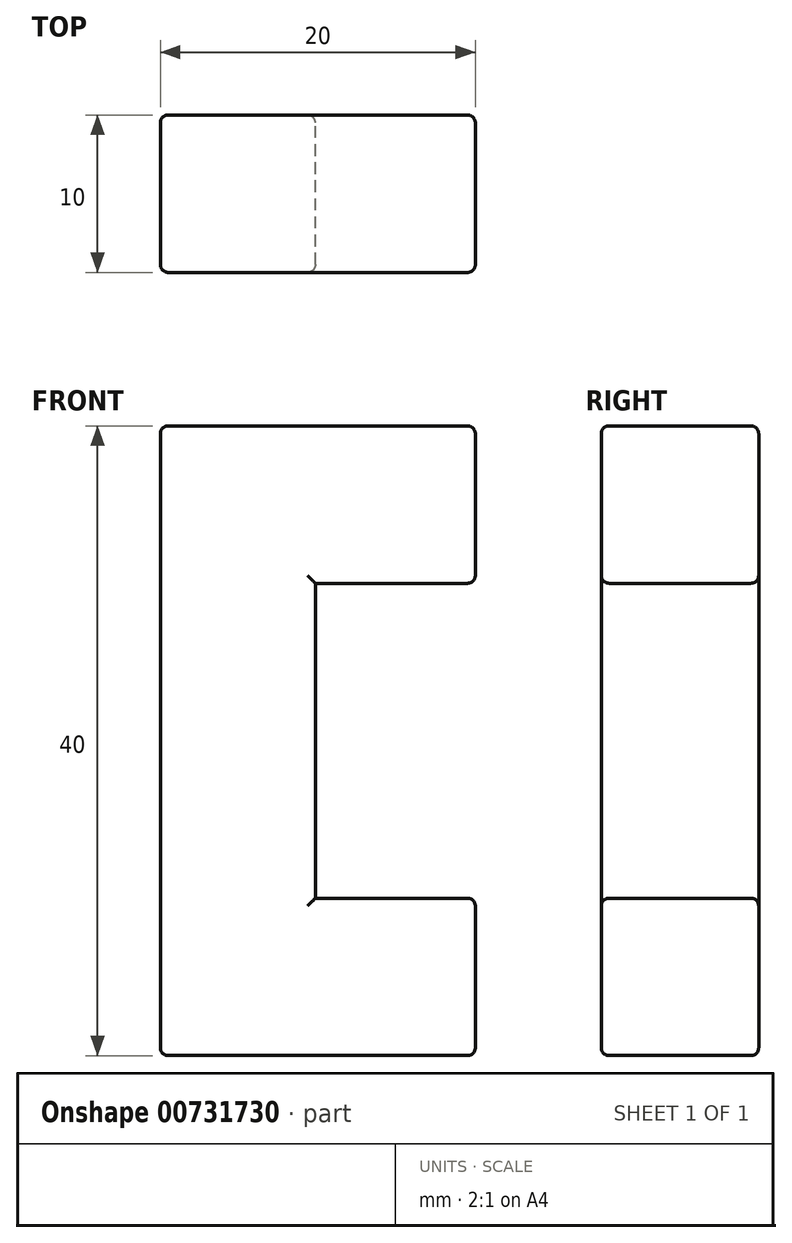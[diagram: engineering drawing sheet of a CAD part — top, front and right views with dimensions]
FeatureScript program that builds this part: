
annotation { "Feature Type Name" : "Feature", "Feature Type Description" : "" }
export const myFeature = defineFeature(function(context is Context, id is Id, definition is map)
    precondition{}
    {
        {
            var Q0;
            Q0=qCreatedBy(makeId("Front.planeOp"),FACE);
            var sketch = newSketch(context, id + "F0", { "sketchPlane" : qUnion([Q0])});
            skLineSegment(sketch, "E0", {"start": v(-5.43, 14.7) * mm, "end": v(14.57, 14.7) * mm});
            skLineSegment(sketch, "E1", {"start": v(-5.43, 14.7) * mm, "end": v(-5.43, -25.3) * mm});
            skLineSegment(sketch, "E2", {"start": v(14.57, 14.7) * mm, "end": v(14.57, 4.7) * mm});
            skLineSegment(sketch, "E3", {"start": v(4.41, 4.7) * mm, "end": v(14.57, 4.7) * mm});
            skLineSegment(sketch, "E4", {"start": v(4.41, 4.7) * mm, "end": v(4.41, -15.3) * mm});
            skLineSegment(sketch, "E5", {"start": v(4.41, -15.3) * mm, "end": v(14.57, -15.3) * mm});
            skLineSegment(sketch, "E6", {"start": v(14.57, -15.3) * mm, "end": v(14.57, -25.3) * mm});
            skLineSegment(sketch, "E7", {"start": v(-5.43, -25.3) * mm, "end": v(14.57, -25.3) * mm});
            skSolve(sketch);
        }
        {
            var Q0;
            Q0=qSketchRegion(id+"F0",true);
            extrude(context, id + "F1", {"entities" : qUnion([Q0]), "depth" : 10 * mm, "offsetDistance" : 25 * mm});
        }
        {
            var Q0;
            Q0=makeQuery(id+"F1.opExtrude","CAP_FACE",FACE,{"disambiguationData":[OSD([sQuery(id+"F0.wireOp",EDGE,"E0"),sQuery(id+"F0.wireOp",EDGE,"E1"),sQuery(id+"F0.wireOp",EDGE,"E2"),sQuery(id+"F0.wireOp",EDGE,"E3"),sQuery(id+"F0.wireOp",EDGE,"E4"),sQuery(id+"F0.wireOp",EDGE,"E5"),sQuery(id+"F0.wireOp",EDGE,"E6"),sQuery(id+"F0.wireOp",EDGE,"E7")])],"isStart":false});
            fillet(context, id + "F2", {"entities" : qUnion([Q0]), "radius" : 0.5 * mm, "tangentPropagation" : true, "allowEdgeOverflow" : false});
        }
        {
            var Q0;
            Q0=makeQuery(id+"F1.opExtrude","CAP_FACE",FACE,{"disambiguationData":[OSD([sQuery(id+"F0.wireOp",EDGE,"E0"),sQuery(id+"F0.wireOp",EDGE,"E1"),sQuery(id+"F0.wireOp",EDGE,"E2"),sQuery(id+"F0.wireOp",EDGE,"E3"),sQuery(id+"F0.wireOp",EDGE,"E4"),sQuery(id+"F0.wireOp",EDGE,"E5"),sQuery(id+"F0.wireOp",EDGE,"E6"),sQuery(id+"F0.wireOp",EDGE,"E7")])],"isStart":true});
            fillet(context, id + "F3", {"entities" : qUnion([Q0]), "radius" : 0.5 * mm, "tangentPropagation" : true, "allowEdgeOverflow" : false});
        }
        {
            var Q0;
            Q0=makeQuery(id+"F1.opExtrude","SWEPT_FACE",FACE,{"disambiguationData":[OSD([sQuery(id+"F0.wireOp",EDGE,"E6")])]});
            var Q1;
            Q1=makeQuery(id+"F1.opExtrude","SWEPT_FACE",FACE,{"disambiguationData":[OSD([sQuery(id+"F0.wireOp",EDGE,"E7")])]});
            var Q2;
            Q2=makeQuery(id+"F1.opExtrude","SWEPT_FACE",FACE,{"disambiguationData":[OSD([sQuery(id+"F0.wireOp",EDGE,"E2")])]});
            var Q3;
            Q3=makeQuery(id+"F1.opExtrude","SWEPT_FACE",FACE,{"disambiguationData":[OSD([sQuery(id+"F0.wireOp",EDGE,"E0")])]});
            var Q4;
            Q4=makeQuery(id+"F1.opExtrude","SWEPT_FACE",FACE,{"disambiguationData":[OSD([sQuery(id+"F0.wireOp",EDGE,"E1")])]});
            fillet(context, id + "F4", {"entities" : qUnion([Q0, Q1, Q2, Q3, Q4]), "radius" : 0.5 * mm, "tangentPropagation" : true, "allowEdgeOverflow" : false});
        }
    });
